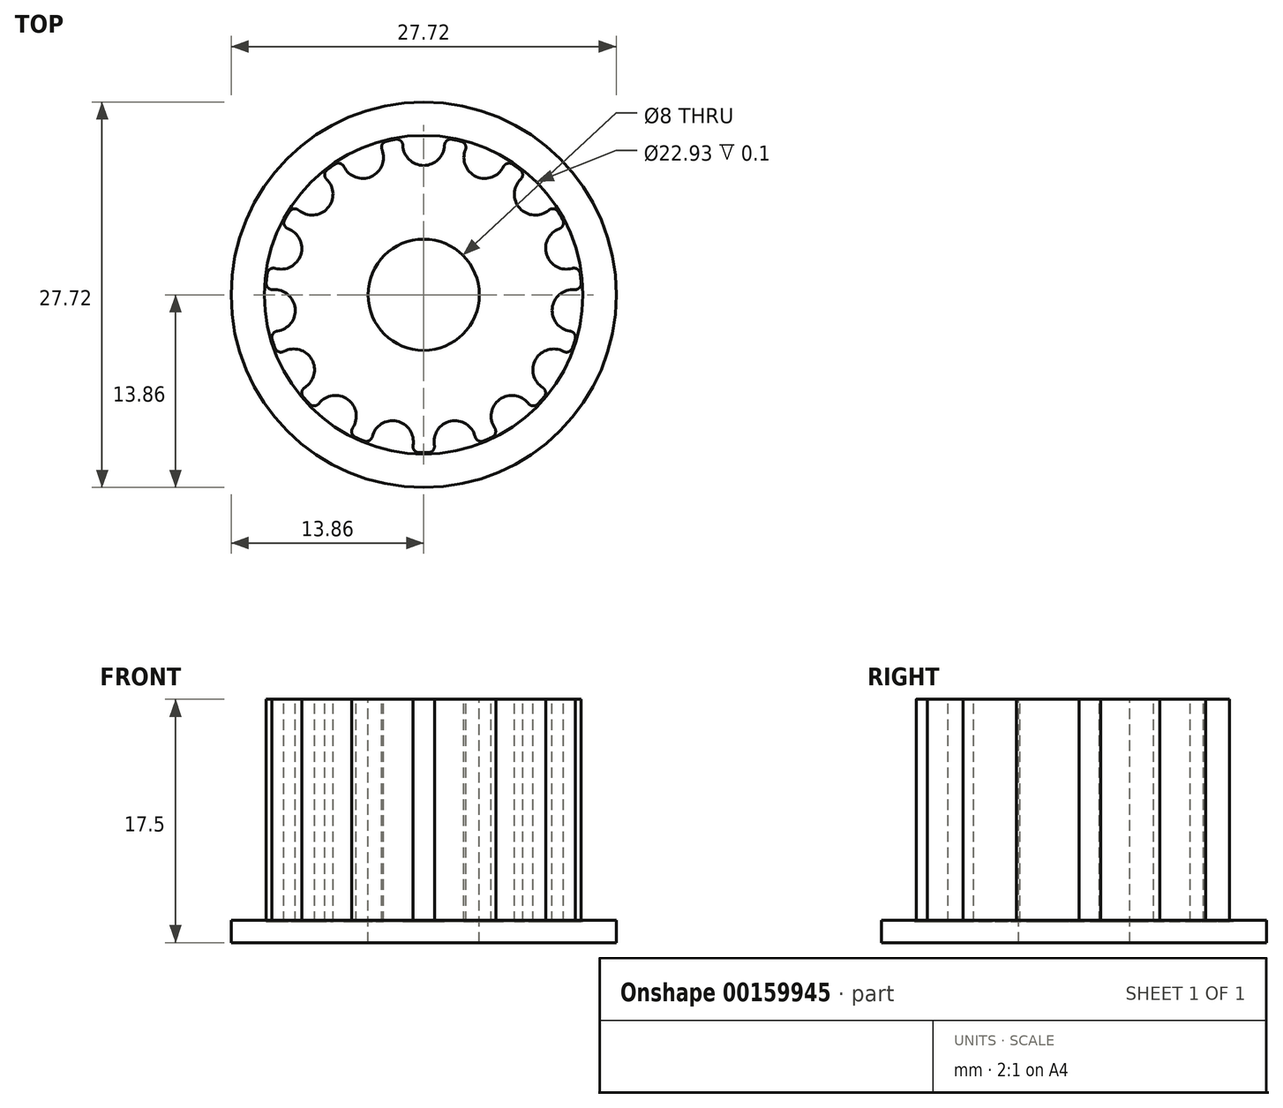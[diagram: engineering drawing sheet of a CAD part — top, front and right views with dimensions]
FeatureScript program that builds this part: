
annotation { "Feature Type Name" : "Feature", "Feature Type Description" : "" }
export const myFeature = defineFeature(function(context is Context, id is Id, definition is map)
    precondition{}
    {
        {
            assignVariable(context, id + "F0", {"name" : "Teeth", "anyValue" : 15});
        }
        {
            assignVariable(context, id + "F1", {"name" : "Width", "anyValue" : 16});
        }
        {
            var Q0;
            Q0=qCreatedBy(makeId("Top.planeOp"),FACE);
            var sketch = newSketch(context, id + "F2", { "sketchPlane" : qUnion([Q0])});
            skCircle(sketch, "E0", {"center": v(0, 0) * mm, "radius": 11.36 * mm});
            skSolve(sketch);
        }
        {
            var Q0;
            Q0=qSketchRegion(id+"F2",true);
            extrude(context, id + "F3", {"entities" : qUnion([Q0]), "depth" : (getVariable(context, 'Width')) * mm});
        }
        {
            var Q0;
            Q0=makeQuery(id+"F3.opExtrude","CAP_FACE",FACE,{"disambiguationData":[OSD([sQuery(id+"F2.wireOp",EDGE,"E0")])],"isStart":false});
            var sketch = newSketch(context, id + "F4", { "sketchPlane" : qUnion([Q0])});
            skCircle(sketch, "E1", {"center": v(0, 0) * mm, "radius": 9.3 * mm, "construction": true});
            skArc(sketch, "E2", {"start": v(-1.5, 10.75) * mm, "mid": v(0, 9.3) * mm, "end": v(1.5, 10.75) * mm});
            skArc(sketch, "E3", {"start": v(2.03, 11.18) * mm, "mid": v(0, 11.36) * mm, "end": v(-2.03, 11.18) * mm});
            skArc(sketch, "E4", {"start": v(-1.5, 10.75) * mm, "mid": v(-1.67, 11.09) * mm, "end": v(-2.03, 11.18) * mm});
            skArc(sketch, "E5", {"start": v(2.03, 11.18) * mm, "mid": v(1.67, 11.09) * mm, "end": v(1.5, 10.75) * mm});
            skSolve(sketch);
        }
        {
            var Q0;
            Q0=makeQuery(id+"F4.imprint","IMPRINT",FACE,{"disambiguationData":[TD([[makeQuery(id+"F4.imprint","IMPRINT",EDGE,{"derivedFrom":sQuery(id+"F4.wireOp",EDGE,"E2")}),1.0]])]});
            var Q1;
            Q1=makeQuery(id+"F3.opExtrude","CAP_FACE",FACE,{"disambiguationData":[OSD([sQuery(id+"F2.wireOp",EDGE,"E0")])],"isStart":true});
            extrude(context, id + "F5", {"entities" : qUnion([Q0]), "operationType" : NewBodyOperationType.REMOVE, "endBound" : BoundingType.UP_TO_SURFACE, "oppositeDirection" : true, "endBoundEntityFace" : qUnion([Q1]), "depth" : 25 * mm});
        }
        {
            var Q0;
            Q0=makeQuery(id+"F5.boolean.opBoolean","COPY",FACE,{"derivedFrom":makeQuery(id+"F5.opExtrude","SWEPT_FACE",FACE,{"disambiguationData":[OSD([sQuery(id+"F4.wireOp",EDGE,"E4")])]})});
            var Q1;
            Q1=makeQuery(id+"F5.boolean.opBoolean","COPY",FACE,{"derivedFrom":makeQuery(id+"F5.opExtrude","SWEPT_FACE",FACE,{"disambiguationData":[OSD([sQuery(id+"F4.wireOp",EDGE,"kHu0Iwj9-o4Cv-DRlk-4OjM-lw9Y4UkXsprA")])]})});
            var Q2;
            Q2=makeQuery(id+"F5.boolean.opBoolean","COPY",FACE,{"derivedFrom":makeQuery(id+"F5.opExtrude","SWEPT_FACE",FACE,{"disambiguationData":[OSD([sQuery(id+"F4.wireOp",EDGE,"E2")])]})});
            var Q3;
            Q3=makeQuery(id+"F5.boolean.opBoolean","COPY",FACE,{"derivedFrom":makeQuery(id+"F5.opExtrude","SWEPT_FACE",FACE,{"disambiguationData":[OSD([sQuery(id+"F4.wireOp",EDGE,"lCBZwTSR-BtAH-iuKv-YoZ4-wjcx4KIexOll")])]})});
            var Q4;
            Q4=makeQuery(id+"F5.boolean.opBoolean","COPY",FACE,{"derivedFrom":makeQuery(id+"F5.opExtrude","SWEPT_FACE",FACE,{"disambiguationData":[OSD([sQuery(id+"F4.wireOp",EDGE,"E5")])]})});
            var Q5;
            Q5=makeQuery(id+"F3.opExtrude","SWEPT_FACE",FACE,{"disambiguationData":[OSD([sQuery(id+"F2.wireOp",EDGE,"E0")])]});
            circularPattern(context, id + "F6", {"faces" : qUnion([Q0, Q1, Q2, Q3, Q4]), "axis" : qUnion([Q5]), "angle" : 360 * degree, "instanceCount" : getVariable(context, 'Teeth'), "equalSpace" : true, "patternType" : PatternType.FACE});
        }
        {
            var Q0;
            Q0=makeQuery(id+"F3.opExtrude","CAP_FACE",FACE,{"disambiguationData":[OSD([sQuery(id+"F2.wireOp",EDGE,"E0")])],"isStart":false});
            var sketch = newSketch(context, id + "F7", { "sketchPlane" : qUnion([Q0])});
            skCircle(sketch, "E6.cCircle", {"center": v(0, 0) * mm, "radius": 4 * mm});
            skLineSegment(sketch, "E6.0", {"start": v(-2.3, 4) * mm, "end": v(2.3, 4) * mm, "construction": true});
            skLineSegment(sketch, "E6.1", {"start": v(2.3, 4) * mm, "end": v(4.62, 0) * mm, "construction": true});
            skLineSegment(sketch, "E6.2", {"start": v(4.62, 0) * mm, "end": v(2.3, -4) * mm, "construction": true});
            skLineSegment(sketch, "E6.3", {"start": v(2.3, -4) * mm, "end": v(-2.3, -4) * mm, "construction": true});
            skLineSegment(sketch, "E6.4", {"start": v(-2.3, -4) * mm, "end": v(-4.62, 0) * mm, "construction": true});
            skLineSegment(sketch, "E6.5", {"start": v(-4.62, 0) * mm, "end": v(-2.3, 4) * mm, "construction": true});
            skPoint(sketch, "E6.0.midPoint", {"position": v(0, 4) * mm});
            skSolve(sketch);
        }
        {
            var Q0;
            Q0=makeQuery(id+"F2.imprint","IMPRINT",FACE,{"disambiguationData":[TD([[makeQuery(id+"F2.imprint","IMPRINT",EDGE,{"derivedFrom":sQuery(id+"F2.wireOp",EDGE,"E0")}),1.0]])]});
            var sketch = newSketch(context, id + "F8", { "sketchPlane" : qUnion([Q0])});
            skCircle(sketch, "E7.0", {"center": v(0, 0) * mm, "radius": 11.36 * mm, "construction": true});
            skCircle(sketch, "E8", {"center": v(0, 0) * mm, "radius": 13.86 * mm});
            skSolve(sketch);
        }
        {
            var Q0;
            Q0=makeQuery(id+"F8.imprint","IMPRINT",FACE,{"disambiguationData":[TD([[makeQuery(id+"F8.imprint","IMPRINT",EDGE,{"derivedFrom":sQuery(id+"F8.wireOp",EDGE,"E8")}),1.0]])]});
            var Q1;
            Q1=makeQuery(id+"F2.imprint","IMPRINT",FACE,{"disambiguationData":[TD([[makeQuery(id+"F2.imprint","IMPRINT",EDGE,{"derivedFrom":sQuery(id+"F2.wireOp",EDGE,"E0")}),1.0]])]});
            extrude(context, id + "F9", {"entities" : qUnion([Q0, Q1]), "operationType" : NewBodyOperationType.ADD, "oppositeDirection" : true, "depth" : 1.5 * mm});
        }
        {
            var Q0;
            Q0=makeQuery(id+"F7.imprint","IMPRINT",FACE,{"disambiguationData":[TD([[makeQuery(id+"F7.imprint","IMPRINT",EDGE,{"derivedFrom":sQuery(id+"F7.wireOp",EDGE,"E6.cCircle")}),1.0]])]});
            extrude(context, id + "F10", {"entities" : qUnion([Q0]), "operationType" : NewBodyOperationType.REMOVE, "endBound" : BoundingType.THROUGH_ALL, "oppositeDirection" : true, "depth" : 25 * mm, "offsetDistance" : 25 * mm});
        }
        {
            var Q0;
            {var subQ0=sQuery(id+"F2.wireOp",EDGE,"E0");Q0=makeQuery(id+"F9.boolean.opBoolean","MERGE",FACE,{"derivedFrom":[makeQuery(id+"F9.opExtrude","CAP_FACE",FACE,{"disambiguationData":[OSD([subQ0])],"isStart":true}),makeQuery(id+"F9.opExtrude","CAP_FACE",FACE,{"disambiguationData":[OSD([subQ0,sQuery(id+"F8.wireOp",EDGE,"E8")])],"isStart":true})]});}
            var sketch = newSketch(context, id + "F11", { "sketchPlane" : qUnion([Q0])});
            skCircle(sketch, "E9.0", {"center": v(0, 0) * mm, "radius": 11.36 * mm, "construction": true});
            skCircle(sketch, "E10.0", {"center": v(0, 0) * mm, "radius": 11.46 * mm});
            skSolve(sketch);
        }
        {
            var Q0;
            Q0=makeQuery(id+"F11.imprint","IMPRINT",FACE,{"disambiguationData":[TD([[makeQuery(id+"F11.imprint","IMPRINT",EDGE,{"derivedFrom":sQuery(id+"F11.wireOp",EDGE,"E10.0")}),-1.0]])]});
            extrude(context, id + "F12", {"entities" : qUnion([Q0]), "operationType" : NewBodyOperationType.ADD, "depth" : .1 * mm, "offsetDistance" : 25 * mm});
        }
    });
